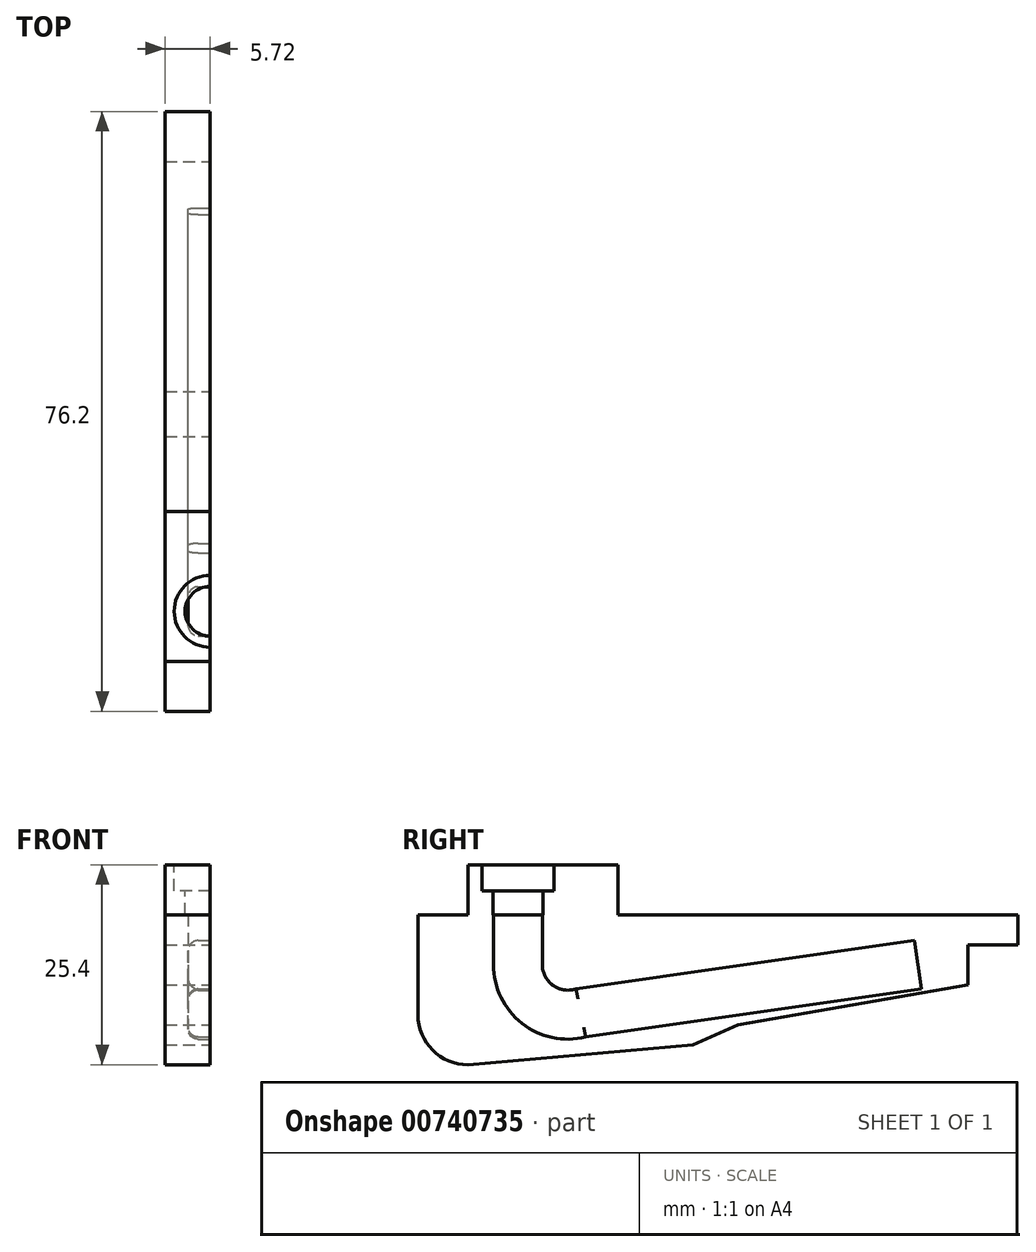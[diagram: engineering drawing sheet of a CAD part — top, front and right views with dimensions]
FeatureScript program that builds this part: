
annotation { "Feature Type Name" : "Feature", "Feature Type Description" : "" }
export const myFeature = defineFeature(function(context is Context, id is Id, definition is map)
    precondition{}
    {
        {
            var Q0;
            Q0=qCreatedBy(makeId("Right.planeOp"),FACE);
            var sketch = newSketch(context, id + "F0", { "sketchPlane" : qUnion([Q0])});
            skLineSegment(sketch, "E0.bottom", {"start": v(0, 0) * mm, "end": v(76.2, 0) * mm});
            skLineSegment(sketch, "E0.top", {"start": v(0, -19.05) * mm, "end": v(76.2, -19.05) * mm});
            skLineSegment(sketch, "E0.left", {"start": v(0, 0) * mm, "end": v(0, -19.05) * mm});
            skLineSegment(sketch, "E0.right", {"start": v(76.2, 0) * mm, "end": v(76.2, -19.05) * mm});
            skSolve(sketch);
        }
        {
            var Q0;
            Q0 = qSketchRegion(id + "F0", true);
            extrude(context, id + "F1", {"entities" : qUnion([Q0]), "depth" : 5.7 * mm, "offsetDistance" : 25.4 * mm});
        }
        {
            var Q0;
            Q0=makeQuery(id+"F1.opExtrude","CAP_FACE",FACE,{"disambiguationData":[OSD([sQuery(id+"F0.wireOp",EDGE,"E0.bottom"),sQuery(id+"F0.wireOp",EDGE,"E0.top"),sQuery(id+"F0.wireOp",EDGE,"E0.left"),sQuery(id+"F0.wireOp",EDGE,"E0.right")])],"isStart":false});
            var sketch = newSketch(context, id + "F2", { "sketchPlane" : qUnion([Q0])});
            skLineSegment(sketch, "E1", {"start": v(0, -12.7) * mm, "end": v(6.35, -12.7) * mm, "construction": true});
            skLineSegment(sketch, "E2", {"start": v(6.35, -12.7) * mm, "end": v(6.35, -19.05) * mm, "construction": true});
            skArc(sketch, "E3", {"start": v(0, -12.7) * mm, "mid": v(1.86, -17.2) * mm, "end": v(6.35, -19.05) * mm});
            skLineSegment(sketch, "E4", {"start": v(76.2, -3.81) * mm, "end": v(69.85, -3.81) * mm});
            skLineSegment(sketch, "E5", {"start": v(69.85, -3.81) * mm, "end": v(69.85, -8.89) * mm});
            skLineSegment(sketch, "E6", {"start": v(69.85, -8.89) * mm, "end": v(40.64, -13.97) * mm});
            skLineSegment(sketch, "E7", {"start": v(40.64, -13.97) * mm, "end": v(34.93, -16.51) * mm});
            skLineSegment(sketch, "E8", {"start": v(34.93, -16.51) * mm, "end": v(6.35, -19.05) * mm});
            skSolve(sketch);
        }
        {
            var Q0;
            Q0=makeQuery(id+"F1.opExtrude","CAP_FACE",FACE,{"disambiguationData":[OSD([sQuery(id+"F0.wireOp",EDGE,"E0.bottom"),sQuery(id+"F0.wireOp",EDGE,"E0.top"),sQuery(id+"F0.wireOp",EDGE,"E0.left"),sQuery(id+"F0.wireOp",EDGE,"E0.right")])],"isStart":false});
            var sketch = newSketch(context, id + "F3", { "sketchPlane" : qUnion([Q0])});
            skLineSegment(sketch, "E9", {"start": v(0, -12.7) * mm, "end": v(6.35, -12.7) * mm, "construction": true});
            skLineSegment(sketch, "E10", {"start": v(6.35, -12.7) * mm, "end": v(6.35, -19.05) * mm, "construction": true});
            skSolve(sketch);
        }
        {
            var Q0;
            {var subQ0=sQuery(id+"F2.wireOp",EDGE,"E4");Q0=makeQuery(id+"F2.imprint","IMPRINT",FACE,{"disambiguationData":[TD([[makeQuery(id+"F2.imprint","IMPRINT",EDGE,{"derivedFrom":subQ0}),1.0]])]});}
            var Q1;
            {var subQ0=sQuery(id+"F2.wireOp",EDGE,"E3");Q1=makeQuery(id+"F2.imprint","IMPRINT",FACE,{"disambiguationData":[TD([[makeQuery(id+"F2.imprint","IMPRINT",EDGE,{"derivedFrom":subQ0}),-1.0]])]});}
            extrude(context, id + "F4", {"entities" : qUnion([Q0, Q1]), "operationType" : NewBodyOperationType.REMOVE, "oppositeDirection" : true, "depth" : 25.4 * mm, "offsetDistance" : 25.4 * mm});
        }
        {
            var Q0;
            Q0=makeQuery(id+"F3.imprint","IMPRINT",FACE,{"disambiguationData":[TD([[makeQuery(id+"F3.imprint","IMPRINT",EDGE,{"derivedFrom":makeQuery(id+"F1.opExtrude","CAP_EDGE",EDGE,{"disambiguationData":[OSD([sQuery(id+"F0.wireOp",EDGE,"E0.bottom")])],"isStart":false})}),-1.0]])]});
            var sketch = newSketch(context, id + "F5", { "sketchPlane" : qUnion([Q0])});
            skLineSegment(sketch, "E11", {"start": v(0, -6.35) * mm, "end": v(63.5, -6.35) * mm, "construction": true});
            skLineSegment(sketch, "E12", {"start": v(0, -12.7) * mm, "end": v(38.1, -12.7) * mm, "construction": true});
            skLineSegment(sketch, "E13", {"start": v(12.7, 0) * mm, "end": v(12.7, -12.7) * mm, "construction": true});
            skLineSegment(sketch, "E14", {"start": v(19.05, 0) * mm, "end": v(19.05, -12.7) * mm, "construction": true});
            skArc(sketch, "E15", {"start": v(12.7, -6.35) * mm, "mid": v(15.19, -11.4) * mm, "end": v(20.7, -12.48) * mm});
            skLineSegment(sketch, "E16", {"start": v(12.7, -6.35) * mm, "end": v(12.7, 0) * mm});
            skLineSegment(sketch, "E17", {"start": v(20.7, -12.48) * mm, "end": v(63.5, -6.35) * mm});
            skSolve(sketch);
        }
        {
            var Q0;
            Q0=qCreatedBy(makeId("Right.planeOp"),FACE);
            var sketch = newSketch(context, id + "F6", { "sketchPlane" : qUnion([Q0])});
            skLineSegment(sketch, "E18.bottom", {"start": v(6.35, 0) * mm, "end": v(25.4, 0) * mm});
            skLineSegment(sketch, "E18.top", {"start": v(6.35, 6.35) * mm, "end": v(25.4, 6.35) * mm});
            skLineSegment(sketch, "E18.left", {"start": v(6.35, 0) * mm, "end": v(6.35, 6.35) * mm});
            skLineSegment(sketch, "E18.right", {"start": v(25.4, 0) * mm, "end": v(25.4, 6.35) * mm});
            skSolve(sketch);
        }
        {
            var Q0;
            Q0 = qSketchRegion(id + "F6", true);
            extrude(context, id + "F7", {"entities" : qUnion([Q0]), "operationType" : NewBodyOperationType.ADD, "depth" : 5.7 * mm, "offsetDistance" : 25.4 * mm});
        }
        {
            var Q0;
            {var subQ0=sQuery(id+"F0.wireOp",EDGE,"E0.left");var subQ7=sQuery(id+"F0.wireOp",EDGE,"E0.bottom");Q0=makeQuery(id+"F7.boolean.opBoolean","SPLIT",FACE,{"disambiguationData":[TD([makeQuery(id+"F1.opExtrude","SWEPT_FACE",FACE,{"disambiguationData":[OSD([subQ0])]})])],"derivedFrom":makeQuery(id+"F1.opExtrude","SWEPT_FACE",FACE,{"disambiguationData":[OSD([subQ7])]})});}
            var sketch = newSketch(context, id + "F8", { "sketchPlane" : qUnion([Q0])});
            skLineSegment(sketch, "E19.bottom", {"start": v(4.2, 15.81) * mm, "end": v(8.5, 15.81) * mm});
            skLineSegment(sketch, "E19.top", {"start": v(4.2, 9.59) * mm, "end": v(8.5, 9.59) * mm});
            skLineSegment(sketch, "E19.left", {"start": v(2.92, 14.54) * mm, "end": v(2.92, 10.86) * mm});
            skLineSegment(sketch, "E19.right", {"start": v(8.5, 15.81) * mm, "end": v(8.5, 9.59) * mm});
            skPoint(sketch, "E19.middle", {"position": v(5.71, 12.7) * mm});
            skPoint(sketch, "E20.visualSharp", {"position": v(2.92, 15.81) * mm});
            skArc(sketch, "E20.filletArc", {"start": v(4.2, 15.81) * mm, "mid": v(3.3, 15.44) * mm, "end": v(2.92, 14.54) * mm});
            skPoint(sketch, "E21.visualSharp", {"position": v(2.92, 9.59) * mm});
            skArc(sketch, "E21.filletArc", {"start": v(2.92, 10.86) * mm, "mid": v(3.3, 9.96) * mm, "end": v(4.2, 9.59) * mm});
            skSolve(sketch);
        }
        {
            var Q0;
            Q0 = qSketchRegion(id + "F8", true);
            var Q1;
            Q1=sQuery(id+"F5.wireOp",EDGE,"E16");
            var Q2;
            Q2=sQuery(id+"F5.wireOp",EDGE,"E15");
            var Q3;
            Q3=sQuery(id+"F5.wireOp",EDGE,"E17");
            sweep(context, id + "F9", {"operationType" : NewBodyOperationType.REMOVE, "profiles" : qUnion([Q0]), "path" : qUnion([Q1, Q2, Q3])});
        }
        {
            var Q0;
            Q0=makeQuery(id+"F7.opExtrude","SWEPT_FACE",FACE,{"disambiguationData":[OSD([sQuery(id+"F6.wireOp",EDGE,"E18.top")])]});
            var sketch = newSketch(context, id + "F10", { "sketchPlane" : qUnion([Q0])});
            skCircle(sketch, "E22", {"center": v(5.72, 12.7) * mm, "radius": 4.57 * mm});
            skSolve(sketch);
        }
        {
            var Q0;
            Q0 = qSketchRegion(id + "F10", true);
            extrude(context, id + "F11", {"entities" : qUnion([Q0]), "operationType" : NewBodyOperationType.REMOVE, "oppositeDirection" : true, "depth" : 3.3 * mm, "offsetDistance" : 25.4 * mm});
        }
        {
            var Q0;
            Q0=makeQuery(id+"F11.boolean.opBoolean","COPY",FACE,{"derivedFrom":makeQuery(id+"F11.opExtrude","CAP_FACE",FACE,{"disambiguationData":[OSD([sQuery(id+"F10.wireOp",EDGE,"E22")])],"isStart":false})});
            var sketch = newSketch(context, id + "F12", { "sketchPlane" : qUnion([Q0])});
            skCircle(sketch, "E23", {"center": v(5.72, 12.7) * mm, "radius": 3.18 * mm});
            skSolve(sketch);
        }
        {
            var Q0;
            Q0 = qSketchRegion(id + "F12", true);
            extrude(context, id + "F13", {"entities" : qUnion([Q0]), "operationType" : NewBodyOperationType.REMOVE, "oppositeDirection" : true, "depth" : 3.05 * mm, "offsetDistance" : 25.4 * mm});
        }
    });
